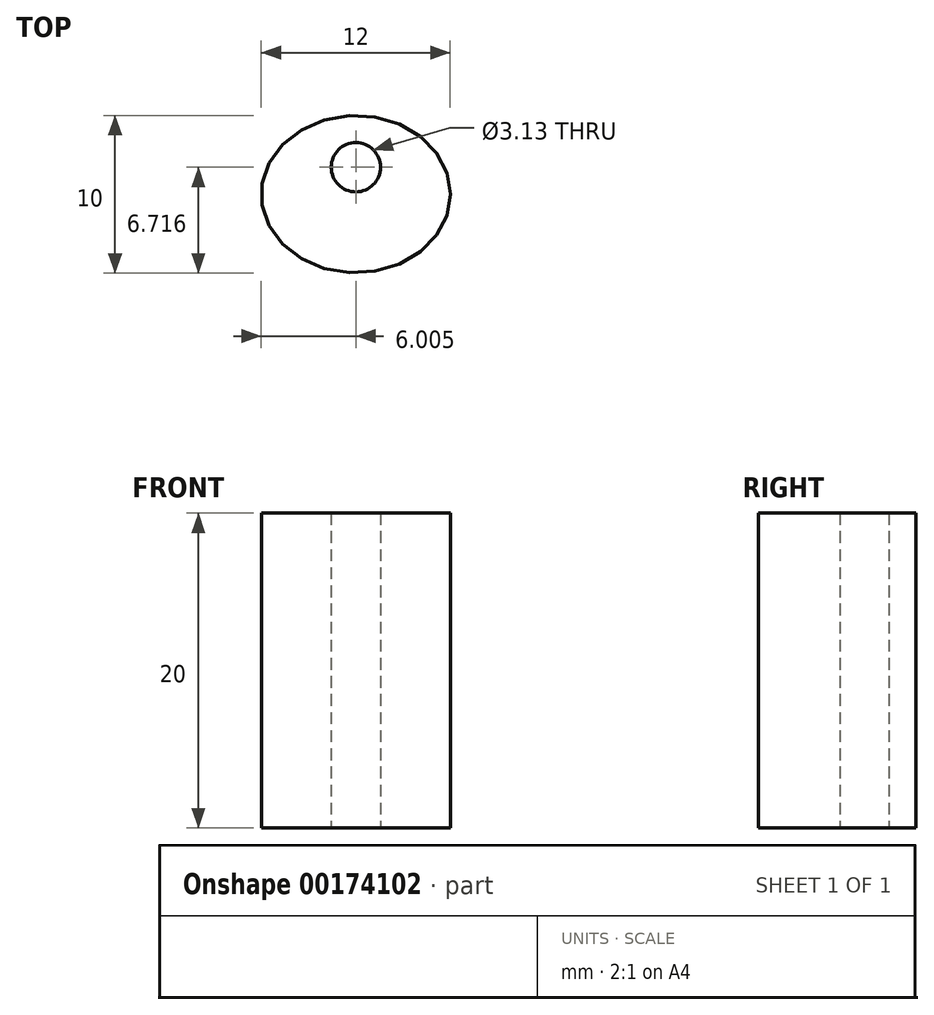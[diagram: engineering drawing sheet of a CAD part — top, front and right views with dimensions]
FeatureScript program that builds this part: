
annotation { "Feature Type Name" : "Feature", "Feature Type Description" : "" }
export const myFeature = defineFeature(function(context is Context, id is Id, definition is map)
    precondition{}
    {
        {
            var Q0;
            Q0=qCreatedBy(makeId("Top.planeOp"),FACE);
            var sketch = newSketch(context, id + "F0", { "sketchPlane" : qUnion([Q0])});
            skEllipse(sketch, "E0", {"center": v(-8.3, 9.52) * mm, "majorRadius": 6 * mm, "minorRadius": 5 * mm, "majorAxis": v(1, 0)});
            skCircle(sketch, "E1", {"center": v(-8.3, 11.24) * mm, "radius": 1.57 * mm});
            skSolve(sketch);
        }
        {
            var Q0;
            Q0=makeQuery(id+"F0.imprint","IMPRINT",FACE,{"disambiguationData":[TD([[makeQuery(id+"F0.imprint","IMPRINT",EDGE,{"derivedFrom":sQuery(id+"F0.wireOp",EDGE,"E0")}),1.0]])]});
            extrude(context, id + "F1", {"entities" : qUnion([Q0]), "depth" : 20 * mm});
        }
    });
